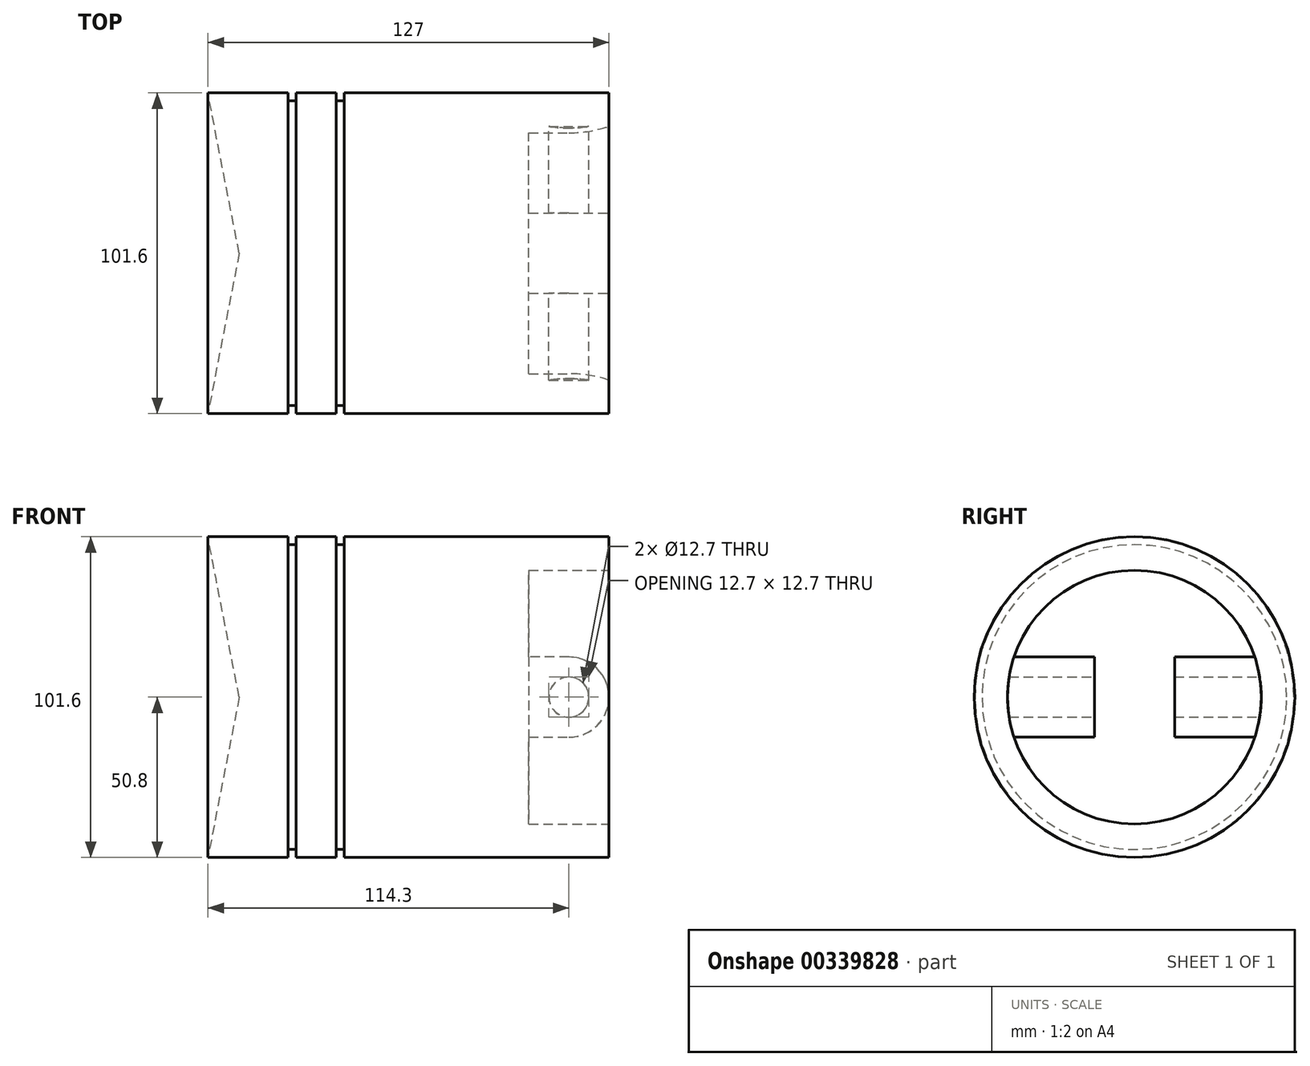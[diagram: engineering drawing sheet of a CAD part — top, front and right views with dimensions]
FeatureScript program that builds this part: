
annotation { "Feature Type Name" : "Feature", "Feature Type Description" : "" }
export const myFeature = defineFeature(function(context is Context, id is Id, definition is map)
    precondition{}
    {
        {
            var Q0;
            Q0=qCreatedBy(makeId("Front.planeOp"),FACE);
            var sketch = newSketch(context, id + "F0", { "sketchPlane" : qUnion([Q0])});
            skLineSegment(sketch, "E0", {"start": v(0, 0) * mm, "end": v(0, 50.8) * mm});
            skLineSegment(sketch, "E1", {"start": v(0, 50.8) * mm, "end": v(0, 50.8) * mm});
            skLineSegment(sketch, "E2", {"start": v(0, 0) * mm, "end": v(127, 0) * mm});
            skLineSegment(sketch, "E3", {"start": v(127, 0) * mm, "end": v(127, 50.8) * mm});
            skLineSegment(sketch, "E4", {"start": v(127, 50.8) * mm, "end": v(43.18, 50.8) * mm});
            skLineSegment(sketch, "E5", {"start": v(43.18, 50.8) * mm, "end": v(43.18, 48.26) * mm});
            skLineSegment(sketch, "E6", {"start": v(43.18, 48.26) * mm, "end": v(40.64, 48.26) * mm});
            skLineSegment(sketch, "E7", {"start": v(40.64, 48.26) * mm, "end": v(40.64, 50.8) * mm});
            skLineSegment(sketch, "E8", {"start": v(40.64, 50.8) * mm, "end": v(27.94, 50.8) * mm});
            skLineSegment(sketch, "E9", {"start": v(27.94, 50.8) * mm, "end": v(27.94, 48.26) * mm});
            skLineSegment(sketch, "E10", {"start": v(27.94, 48.26) * mm, "end": v(25.4, 48.26) * mm});
            skLineSegment(sketch, "E11", {"start": v(25.4, 48.26) * mm, "end": v(25.4, 50.8) * mm});
            skLineSegment(sketch, "E12", {"start": v(25.4, 50.8) * mm, "end": v(0, 50.8) * mm});
            skLineSegment(sketch, "E13", {"start": v(-26.7, 0) * mm, "end": v(0, 0) * mm, "construction": true});
            skPoint(sketch, "E14.MirrorCS.end.orphan", {"position": v(43.18, -50.8) * mm});
            skPoint(sketch, "E14.MirrorCS.start.orphan", {"position": v(127, -50.8) * mm});
            skPoint(sketch, "E15.MirrorCS.start.orphan", {"position": v(127, 0) * mm});
            skPoint(sketch, "E16.MirrorCS.end.orphan", {"position": v(0, -50.8) * mm});
            skPoint(sketch, "E16.MirrorCS.start.orphan", {"position": v(25.4, -50.8) * mm});
            skPoint(sketch, "E17.MirrorCS.start.orphan", {"position": v(0, 0) * mm});
            skPoint(sketch, "E18.MirrorCS.end.orphan", {"position": v(27.94, -50.8) * mm});
            skPoint(sketch, "E18.MirrorCS.start.orphan", {"position": v(40.64, -50.8) * mm});
            skPoint(sketch, "E19.MirrorCS.end.orphan", {"position": v(40.64, -48.26) * mm});
            skPoint(sketch, "E19.MirrorCS.start.orphan", {"position": v(43.18, -48.26) * mm});
            skPoint(sketch, "E20.MirrorCS.end.orphan", {"position": v(27.94, -48.26) * mm});
            skPoint(sketch, "E21.MirrorCS.end.orphan", {"position": v(25.4, -48.26) * mm});
            skLineSegment(sketch, "E22.trimOffspring", {"start": v(127, 0) * mm, "end": v(170.85, 0) * mm, "construction": true});
            skPoint(sketch, "E23", {"position": v(104.24, -9.85) * mm});
            skPoint(sketch, "E24", {"position": v(90.7, -25.37) * mm});
            skSolve(sketch);
        }
        {
            var Q0;
            Q0=makeQuery(id+"F0.imprint","IMPRINT",FACE,{"disambiguationData":[TD([[makeQuery(id+"F0.imprint","IMPRINT",EDGE,{"derivedFrom":sQuery(id+"F0.wireOp",EDGE,"E0")}),-1.0]])]});
            var Q1;
            Q1=sQuery(id+"F0.wireOp",EDGE,"E13");
            revolve(context, id + "F1", {"entities" : qUnion([Q0]), "axis" : qUnion([Q1]), "revolveType" : RevolveType.FULL});
        }
        {
            var Q0;
            Q0=makeQuery(id+"F1.opRevolve","SWEPT_FACE",FACE,{"disambiguationData":[OSD([sQuery(id+"F0.wireOp",EDGE,"E3")])]});
            var sketch = newSketch(context, id + "F2", { "sketchPlane" : qUnion([Q0])});
            skCircle(sketch, "E25", {"center": v(0, 0) * mm, "radius": 40.19 * mm});
            skSolve(sketch);
        }
        {
            var Q0;
            Q0=makeQuery(id+"F2.imprint","IMPRINT",FACE,{"disambiguationData":[TD([[makeQuery(id+"F2.imprint","IMPRINT",EDGE,{"derivedFrom":sQuery(id+"F2.wireOp",EDGE,"E25")}),1.0]])]});
            extrude(context, id + "F3", {"entities" : qUnion([Q0]), "operationType" : NewBodyOperationType.REMOVE, "oppositeDirection" : true, "depth" : 25.4 * mm});
        }
        {
            var Q0;
            Q0=qCreatedBy(makeId("Front.planeOp"),FACE);
            var sketch = newSketch(context, id + "F4", { "sketchPlane" : qUnion([Q0])});
            skLineSegment(sketch, "E26", {"start": v(0, 0) * mm, "end": v(114.3, 0) * mm, "construction": true});
            skLineSegment(sketch, "E27", {"start": v(114.3, 0) * mm, "end": v(114.3, 12.7) * mm, "construction": true});
            skLineSegment(sketch, "E28.MirrorCS", {"start": v(114.3, 0) * mm, "end": v(114.3, -12.7) * mm, "construction": true});
            skArc(sketch, "E29", {"start": v(114.3, -12.7) * mm, "mid": v(127, 0) * mm, "end": v(114.3, 12.7) * mm});
            skLineSegment(sketch, "E30", {"start": v(114.3, 12.7) * mm, "end": v(101.6, 12.7) * mm});
            skLineSegment(sketch, "E31", {"start": v(101.6, 12.7) * mm, "end": v(101.6, -12.7) * mm});
            skLineSegment(sketch, "E32", {"start": v(101.6, -12.7) * mm, "end": v(114.3, -12.7) * mm});
            skCircle(sketch, "E33", {"center": v(114.3, 0) * mm, "radius": 6.35 * mm});
            skSolve(sketch);
        }
        {
            var Q0;
            Q0=makeQuery(id+"F4.imprint","IMPRINT",FACE,{"disambiguationData":[TD([[makeQuery(id+"F4.imprint","IMPRINT",EDGE,{"derivedFrom":sQuery(id+"F4.wireOp",EDGE,"E29")}),1.0]])]});
            extrude(context, id + "F5", {"entities" : qUnion([Q0]), "operationType" : NewBodyOperationType.ADD, "depth" : 48.26 * mm, "hasSecondDirection" : true, "secondDirectionOppositeDirection" : true, "secondDirectionDepth" : 48.26 * mm});
        }
        {
            var Q0;
            Q0 = qSketchRegion(id + "F4", true);
            extrude(context, id + "F6", {"entities" : qUnion([Q0]), "operationType" : NewBodyOperationType.REMOVE, "oppositeDirection" : true, "depth" : 12.7 * mm, "hasSecondDirection" : true, "secondDirectionOppositeDirection" : false, "secondDirectionDepth" : 12.7 * mm});
        }
        {
            var Q0;
            Q0=qCreatedBy(makeId("Front.planeOp"),FACE);
            var sketch = newSketch(context, id + "F7", { "sketchPlane" : qUnion([Q0])});
            skLineSegment(sketch, "E34", {"start": v(0, 0) * mm, "end": v(0, 50.53) * mm});
            skLineSegment(sketch, "E35", {"start": v(0, 50.53) * mm, "end": v(9.89, 0) * mm});
            skLineSegment(sketch, "E36", {"start": v(9.89, 0) * mm, "end": v(0, 0) * mm});
            skSolve(sketch);
        }
        {
            var Q0;
            Q0 = qSketchRegion(id + "F7", true);
            var Q1;
            Q1=sQuery(id+"F7.wireOp",EDGE,"E36");
            revolve(context, id + "F8", {"operationType" : NewBodyOperationType.REMOVE, "entities" : qUnion([Q0]), "axis" : qUnion([Q1]), "revolveType" : RevolveType.FULL, "oppositeDirection" : true});
        }
    });
